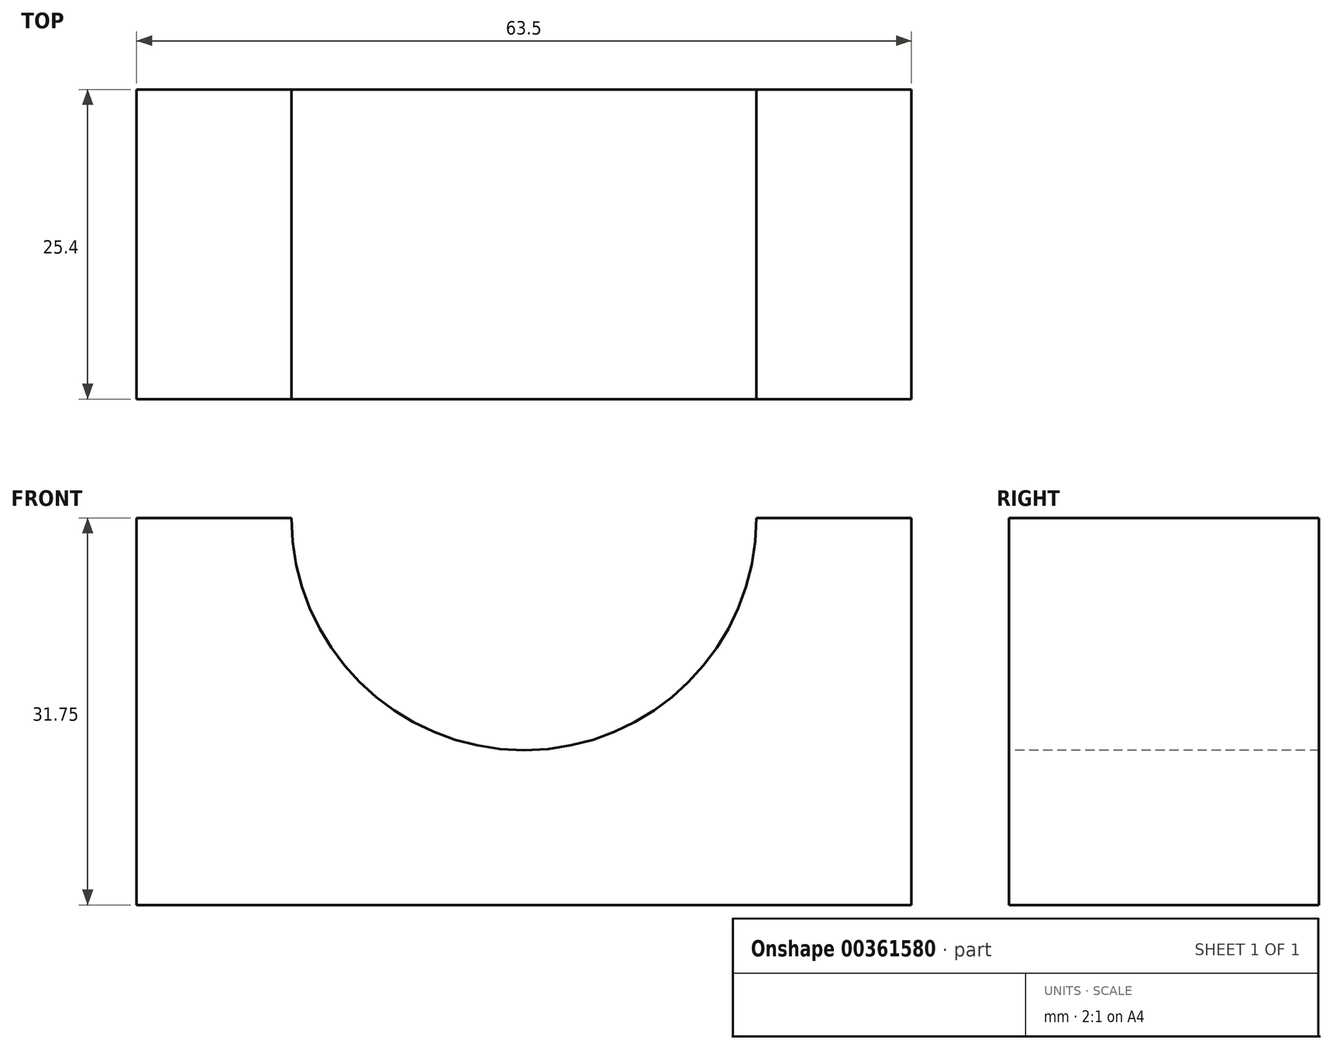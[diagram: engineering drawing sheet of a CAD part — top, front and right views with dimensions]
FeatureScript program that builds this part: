
annotation { "Feature Type Name" : "Feature", "Feature Type Description" : "" }
export const myFeature = defineFeature(function(context is Context, id is Id, definition is map)
    precondition{}
    {
        {
            var Q0;
            Q0=qCreatedBy(makeId("Front.planeOp"),FACE);
            var sketch = newSketch(context, id + "F0", { "sketchPlane" : qUnion([Q0])});
            skLineSegment(sketch, "E0", {"start": v(0, 0) * mm, "end": v(63.5, 0) * mm});
            skLineSegment(sketch, "E1", {"start": v(63.5, 0) * mm, "end": v(63.5, 31.75) * mm});
            skLineSegment(sketch, "E2", {"start": v(63.5, 31.75) * mm, "end": v(0, 31.75) * mm});
            skLineSegment(sketch, "E3", {"start": v(0, 31.75) * mm, "end": v(0, 0) * mm});
            skSolve(sketch);
        }
        {
            var Q0;
            Q0=makeQuery(id+"F0.imprint","IMPRINT",FACE,{"disambiguationData":[TD([[makeQuery(id+"F0.imprint","IMPRINT",EDGE,{"derivedFrom":sQuery(id+"F0.wireOp",EDGE,"E0")}),1.0]])]});
            extrude(context, id + "F1", {"entities" : qUnion([Q0]), "depth" : 25.4 * mm});
        }
        {
            var Q0;
            Q0=makeQuery(id+"F1.opExtrude","CAP_FACE",FACE,{"disambiguationData":[OSD([sQuery(id+"F0.wireOp",EDGE,"E0"),sQuery(id+"F0.wireOp",EDGE,"E1"),sQuery(id+"F0.wireOp",EDGE,"E2"),sQuery(id+"F0.wireOp",EDGE,"E3")])],"isStart":false});
            var sketch = newSketch(context, id + "F2", { "sketchPlane" : qUnion([Q0])});
            skArc(sketch, "E4", {"start": v(12.7, 31.75) * mm, "mid": v(31.75, 12.7) * mm, "end": v(50.8, 31.75) * mm});
            skSolve(sketch);
        }
        {
            var Q0;
            {var subQ0=sQuery(id+"F2.wireOp",EDGE,"E4");Q0=makeQuery(id+"F2.imprint","IMPRINT",FACE,{"disambiguationData":[TD([[makeQuery(id+"F2.imprint","IMPRINT",EDGE,{"derivedFrom":subQ0}),1.0]])]});}
            extrude(context, id + "F3", {"entities" : qUnion([Q0]), "operationType" : NewBodyOperationType.REMOVE, "oppositeDirection" : true, "depth" : 25.4 * mm});
        }
    });
